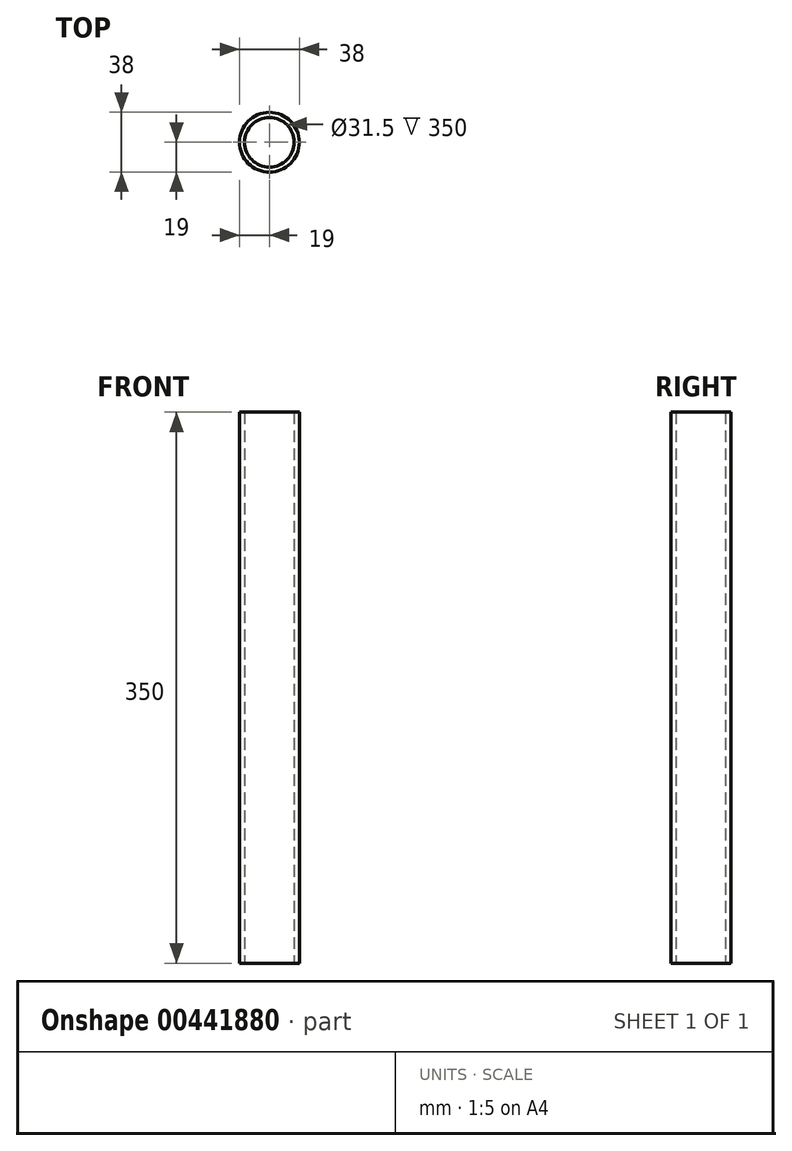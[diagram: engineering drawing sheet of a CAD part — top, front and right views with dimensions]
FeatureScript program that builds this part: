
annotation { "Feature Type Name" : "Feature", "Feature Type Description" : "" }
export const myFeature = defineFeature(function(context is Context, id is Id, definition is map)
    precondition{}
    {
        {
            var Q0;
            Q0=qCreatedBy(makeId("Top.planeOp"),FACE);
            var sketch = newSketch(context, id + "F0", { "sketchPlane" : qUnion([Q0])});
            skCircle(sketch, "E0", {"center": v(0, 0) * mm, "radius": 19 * mm});
            skCircle(sketch, "E1.0", {"center": v(0, 0) * mm, "radius": 15.75 * mm});
            skSolve(sketch);
        }
        {
            var Q0;
            Q0 = qSketchRegion(id + "F0", true);
            extrude(context, id + "F1", {"entities" : qUnion([Q0]), "depth" : 350 * mm});
        }
    });
